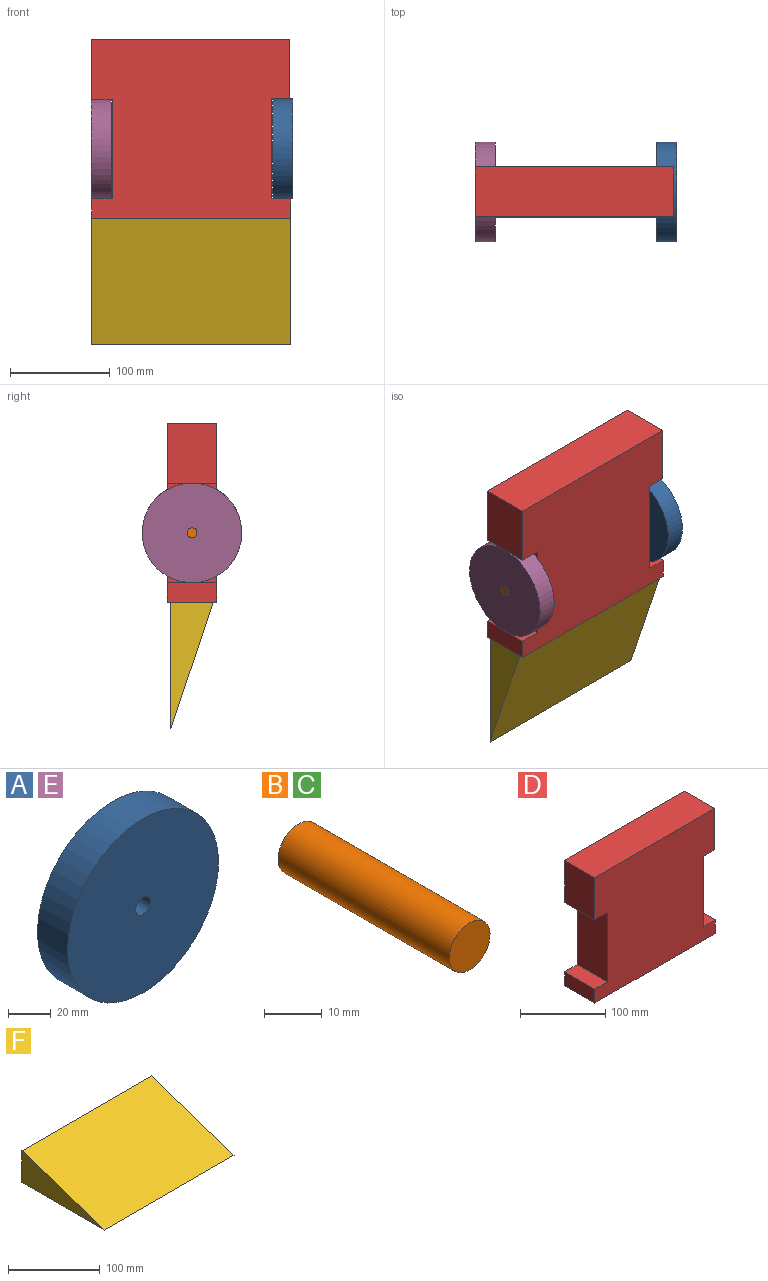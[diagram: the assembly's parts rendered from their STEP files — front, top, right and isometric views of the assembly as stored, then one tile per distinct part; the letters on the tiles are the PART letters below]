
ASSEMBLY  parts=6 mates=5
PART A: 4 faces, bbox 100x20x100 mm
  f0: cylinder r=50mm len=100mm, axis (0,1,0), area 6283.2mm2, adj f1,f2
  f1: plane 100x100mm, normal (0,-1,0), area 7775.4mm2, adj f0,f3
  f2: plane 100x100mm, normal (0,1,0), area 7775.4mm2, adj f0,f3
  f3: cylinder r=5mm len=20mm, axis (0,1,0), area 628.3mm2, adj f1,f2
PART B: 3 faces, bbox 10x42x10 mm
  f0: cylinder r=5mm len=42mm, axis (0,1,0), area 1319.5mm2, adj f1,f2
  f1: plane 10x10mm, normal (0,-1,0), area 78.5mm2, adj f0
  f2: plane 10x10mm, normal (0,1,0), area 78.5mm2, adj f0
PART C: same geometry as B
PART D: 14 faces, bbox 200.1x50x179.8 mm
  f0: plane 50x19.81mm, normal (-1,0,0), area 990.4mm2, adj f1,f11,f12,f13
  f1: plane 200x50mm, normal (0,0,-1), area 10000mm2, adj f0,f2,f12,f13
  f2: plane 50x19.37mm, normal (1,0,0), area 968.3mm2, adj f1,f3,f12,f13
  f3: plane 50x19.63mm, normal (0,0,1), area 981.7mm2, adj f2,f4,f12,f13
  f4: plane 101.02x50mm, normal (1,0,0), area 5051.1mm2, adj f3,f5,f12,f13
  f5: plane 50x18.83mm, normal (0,0,-1), area 941.5mm2, adj f4,f6,f12,f13
  f6: plane 59.36x50mm, normal (1,0,0), area 2968.1mm2, adj f5,f7,f12,f13
  f7: plane 199.29x50mm, normal (0,0,1), area 9964.5mm2, adj f6,f8,f12,f13
  f8: plane 60.28x50mm, normal (-1,0,0), area 3014mm2, adj f7,f9,f12,f13
  f9: plane 50x20.92mm, normal (0,0,-1), area 1046.1mm2, adj f8,f10,f12,f13
  f10: plane 99.66x50mm, normal (-1,0,0), area 4983.2mm2, adj f9,f11,f12,f13
  f11: plane 50x20.83mm, normal (0,0,1), area 1041.5mm2, adj f0,f10,f12,f13
  f12: plane 200.09x179.75mm, normal (0,-1,0), area 31848.8mm2, adj f0,f1,f2,f3,f4,f5,f6,f7
  f13: plane 200.09x179.75mm, normal (0,1,0), area 31848.8mm2, adj f0,f1,f2,f3,f4,f5,f6,f7
PART E: same geometry as A
PART F: 5 faces, bbox 200x127x42.4 mm
  f0: plane 200x42.45mm, normal (0,1,0), area 8489.8mm2, adj f1,f2,f3,f4
  f1: plane 200x127mm, normal (0,-0.32,0.95), area 26781.3mm2, adj f0,f2,f3,f4
  f2: plane 200x127mm, normal (0,0,-1), area 25400mm2, adj f0,f1,f3,f4
  f3: plane 127x42.45mm, normal (1,0,0), area 2695.5mm2, adj f0,f1,f2
  f4: plane 127x42.45mm, normal (-1,0,0), area 2695.5mm2, adj f0,f1,f2
PLACE A rot(axis=(0,0,-1),90deg) t=(101.89,-6.59,-1.19)mm
PLACE B rot(axis=(0.58,-0.58,0.58),120deg) t=(-100.17,-6.59,-1.43)mm fixed
PLACE C rot(axis=(-0.58,-0.58,-0.58),120deg) t=(101.37,-6.59,-1.19)mm fixed
PLACE D t=(0,18.41,3.68)mm fixed
PLACE E rot(axis=(0.57,-0.57,0.58),119.5deg) t=(-100.16,-6.59,-1.43)mm
PLACE F rot(axis=(1,0,0),90deg) t=(-175.89,14.64,-71.07)mm
MATE cylindrical E.f0 <-> D.f10  axis (-1,0,0) through (-90.16,-6.59,-1.43)mm
MATE cylindrical A.f0 <-> C.f0  axis (1,0,0) through (91.89,-6.59,-1.19)mm
MATE parallel D.f1 <-> F.f0  axis (0,0,-1) through (0,-6.59,-71.07)mm
MATE cylindrical B.f0 <-> D.f10  axis (-1,0,0) through (-79.17,-6.59,-1.43)mm
MATE cylindrical D.f4 <-> C.f0  axis (1,0,0) through (80.37,-6.59,-1.19)mm
